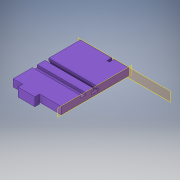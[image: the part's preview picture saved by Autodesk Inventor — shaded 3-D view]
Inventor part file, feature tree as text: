
AUTODESK INVENTOR PART (.ipt)
format: ipt  version: 2018.2 (Build 222227000, 227)  size: 213,504 bytes
history: native  units: in
note: dims shown in document units (in); Inventor stores cm internally (conversion verified against a paired STEP export)
features: extrude x6, sketch x5, mirror x4, split x2, plane x1
ambient origin geometry x8: Origin, YZ Plane, XZ Plane, XY Plane, X Axis, Y Axis, Z Axis, Center Point
bodies: Solid1 (feature_tree)
feature tree (18):
  extrude  "Extrusion1"  Depth=0.375in
  extrude  "Extrusion2"  Depth=0.75in
  mirror  "Mirror1"
  extrude  "Extrusion3"  Depth=7.0in TaperAngle=0.0deg
  extrude  "Extrusion4"  Depth=0.5in TaperAngle=0.0deg
  mirror  "Mirror2"
  extrude  "Extrusion5"  Depth=0.25in
  mirror  "Mirror3"
  extrude  "Extrusion8"  Depth=3.5in
  mirror  "Mirror4"
  split  "Split2"
  plane  "Work Plane1"
  split  "Split3"
  sketch  "Sketch4"  dims[d0=0.375in d1=0.375in]
  sketch  "Sketch6"  dims[d6=2.5in d8=0.75in]
  sketch  "Sketch7"  dims[d9=7.0in d10=14.0in d11=0.0in]
  sketch  "Sketch9"  dims[d12=0.875in d13=0.5in d14=0.0in]
  sketch  "Sketch12"  dims[d16=0.5in d18=0.25in d19=3.5in d20=1.0in d21=0.0in d22=1.75in d23=0.9in d24=1.0in d25=0.5in d26=0.0in d28=0.5in d29=0.25in d30=2.0in d31=0.5in d32=0.0in d46=3.5in d47=0.1875in d48=0.25in d49=0.25in d50=0.344in d51=0.5in d52=0.0in d53=-5.25in]
